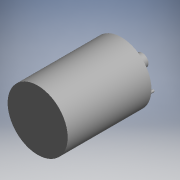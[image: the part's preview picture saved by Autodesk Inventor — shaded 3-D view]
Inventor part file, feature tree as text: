
AUTODESK INVENTOR PART (.ipt)
format: ipt  version: 2019.4 (Build 234330000, 330)  size: 126,464 bytes
history: native  units: mm
features: extrude x4, sketch x3
ambient origin geometry x8: Origin, YZ Plane, XZ Plane, XY Plane, X Axis, Y Axis, Z Axis, Center Point
bodies: Solid1 (feature_tree)
feature tree (7):
  extrude  "Extrusion1"  Depth=34.0mm TaperAngle=0.0deg
  extrude  "Extrusion2"  Depth=8.5mm TaperAngle=0.0deg
  sketch  "Sketch3"  dims[d6=2.5mm d7=6.5mm d8=8.0mm d9=2.5mm d10=6.5mm d11=8.0mm d12=45.0deg d13=1.0mm d14=1.0mm d15=1.0mm d16=5.0mm d17=0.0mm d18=1.0mm d19=1.0mm d20=1.0mm d21=5.0mm d22=0.0mm]
  extrude  "Extrusion3"  Depth=5.0mm
  extrude  "Extrusion4"  Depth=5.0mm
  sketch  "Sketch1"  dims[d0=24.4mm d1=34.0mm d2=0.0mm]
  sketch  "Sketch2"  dims[d3=5.0mm d4=8.5mm d5=0.0mm]
